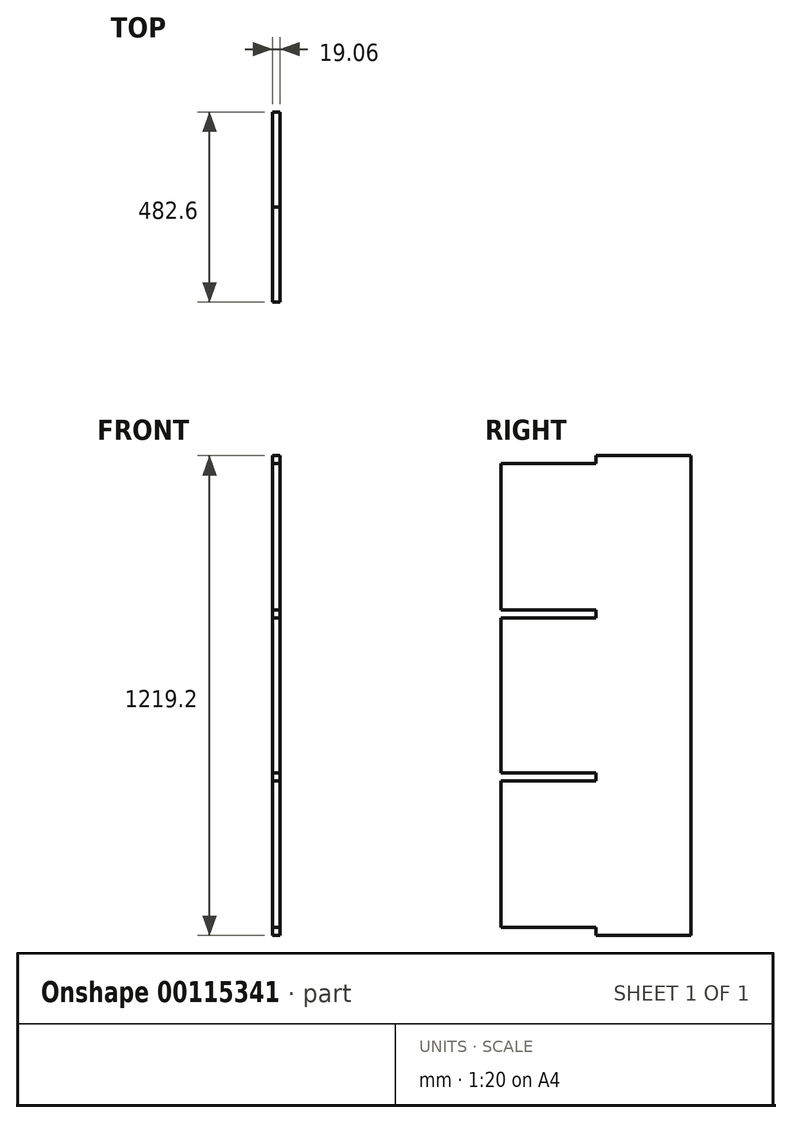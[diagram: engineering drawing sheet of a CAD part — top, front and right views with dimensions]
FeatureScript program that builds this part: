
annotation { "Feature Type Name" : "Feature", "Feature Type Description" : "" }
export const myFeature = defineFeature(function(context is Context, id is Id, definition is map)
    precondition{}
    {
        {
            var Q0;
            Q0=qCreatedBy(makeId("Right.planeOp"),FACE);
            var sketch = newSketch(context, id + "F0", { "sketchPlane" : qUnion([Q0])});
            skLineSegment(sketch, "E0", {"start": v(241.3, 589.28) * mm, "end": v(241.3, -196.85) * mm});
            skLineSegment(sketch, "E1", {"start": v(241.3, -609.6) * mm, "end": v(0, -609.6) * mm});
            skLineSegment(sketch, "E2", {"start": v(-241.3, 589.28) * mm, "end": v(-241.3, 217.17) * mm});
            skLineSegment(sketch, "E3", {"start": v(0, 217.17) * mm, "end": v(-241.3, 217.17) * mm});
            skLineSegment(sketch, "E4", {"start": v(0, 217.17) * mm, "end": v(0, 196.85) * mm});
            skLineSegment(sketch, "E5", {"start": v(0, 196.85) * mm, "end": v(-241.3, 196.85) * mm});
            skLineSegment(sketch, "E6.trimOffspring", {"start": v(-241.3, 196.85) * mm, "end": v(-241.3, -196.85) * mm});
            skLineSegment(sketch, "E7", {"start": v(0, 589.28) * mm, "end": v(0, 609.6) * mm});
            skLineSegment(sketch, "E8", {"start": v(-241.3, -609.6) * mm, "end": v(-241.3, -589.28) * mm});
            skLineSegment(sketch, "E9", {"start": v(-241.3, -589.28) * mm, "end": v(0, -589.28) * mm});
            skLineSegment(sketch, "E10", {"start": v(0, -589.28) * mm, "end": v(0, -609.6) * mm});
            skPoint(sketch, "E11.orphan", {"position": v(241.3, 609.6) * mm});
            skLineSegment(sketch, "E12.trimOffspring", {"start": v(241.3, -217.17) * mm, "end": v(241.3, -609.6) * mm});
            skLineSegment(sketch, "E13", {"start": v(0, 609.6) * mm, "end": v(241.3, 609.6) * mm});
            skLineSegment(sketch, "E14", {"start": v(241.3, 589.28) * mm, "end": v(241.3, 609.6) * mm});
            skLineSegment(sketch, "E15", {"start": v(0, 589.28) * mm, "end": v(-241.3, 589.28) * mm});
            skPoint(sketch, "E16.orphan", {"position": v(-241.3, 609.6) * mm});
            skLineSegment(sketch, "E17", {"start": v(0, -196.85) * mm, "end": v(-241.3, -196.85) * mm});
            skLineSegment(sketch, "E18", {"start": v(0, -217.17) * mm, "end": v(-241.3, -217.17) * mm});
            skLineSegment(sketch, "E19", {"start": v(241.3, -196.85) * mm, "end": v(241.3, -217.17) * mm});
            skLineSegment(sketch, "E20", {"start": v(0, -196.85) * mm, "end": v(0, -217.17) * mm});
            skLineSegment(sketch, "E21.trimOffspring", {"start": v(-241.3, -217.17) * mm, "end": v(-241.3, -589.28) * mm});
            skSolve(sketch);
        }
        {
            var Q0;
            Q0=makeQuery(id+"F0.imprint","IMPRINT",FACE,{"disambiguationData":[TD([[makeQuery(id+"F0.imprint","IMPRINT",EDGE,{"derivedFrom":sQuery(id+"F0.wireOp",EDGE,"E0")}),-1.0]])]});
            extrude(context, id + "F1", {"entities" : qUnion([Q0]), "endBound" : BoundingType.SYMMETRIC, "depth" : 19.05 * mm});
        }
    });
